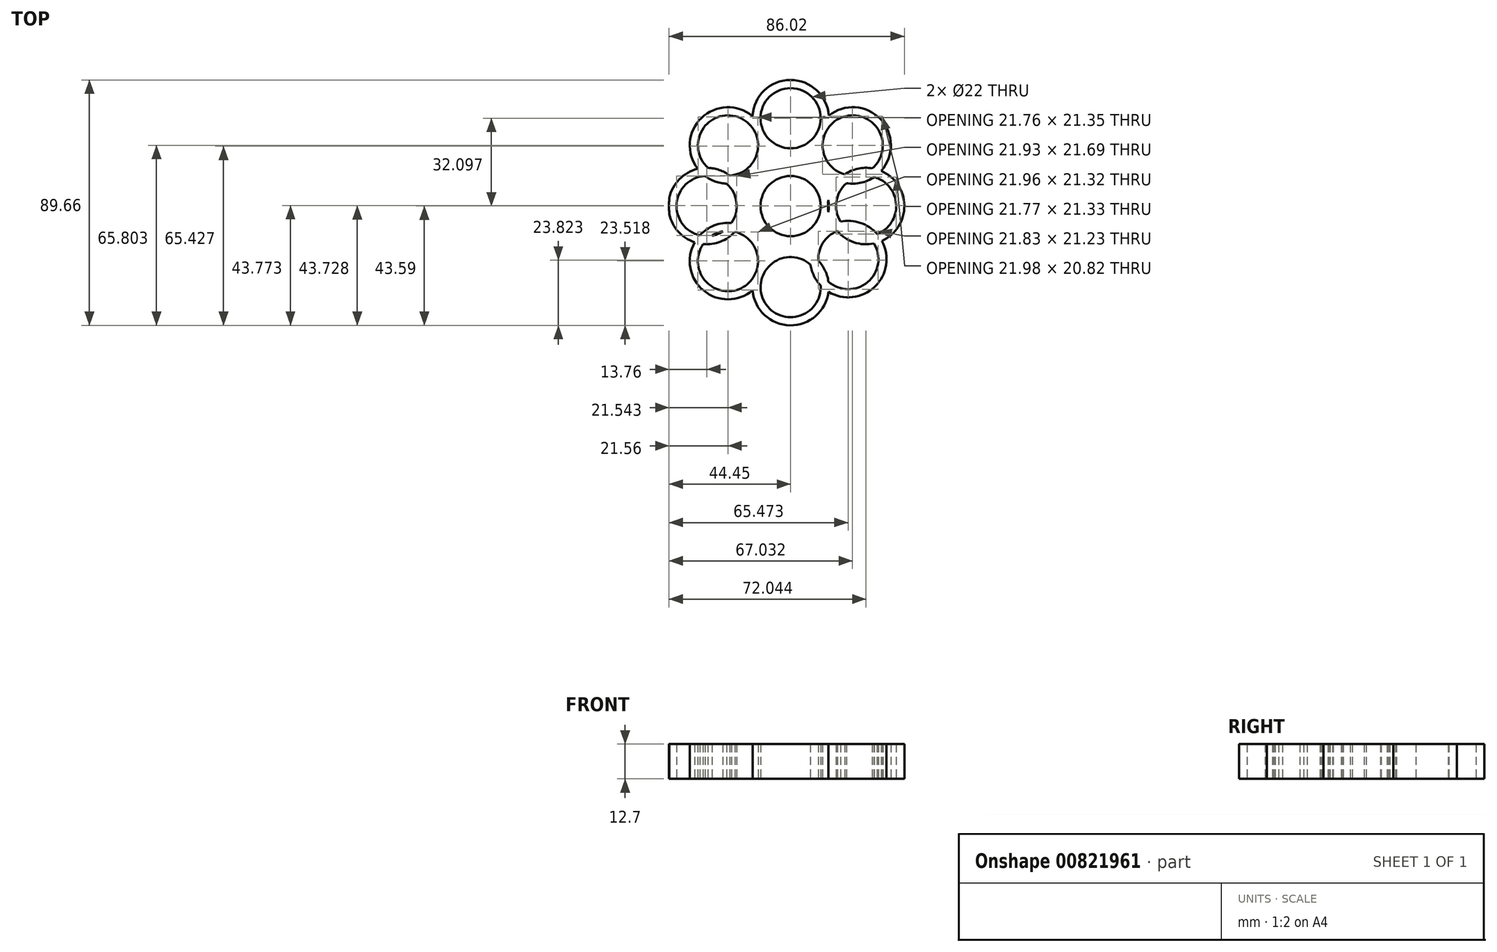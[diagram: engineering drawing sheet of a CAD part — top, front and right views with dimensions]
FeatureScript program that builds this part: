
annotation { "Feature Type Name" : "Feature", "Feature Type Description" : "" }
export const myFeature = defineFeature(function(context is Context, id is Id, definition is map)
    precondition{}
    {
        {
            var Q0;
            Q0=qCreatedBy(makeId("Top.planeOp"),FACE);
            var sketch = newSketch(context, id + "F0", { "sketchPlane" : qUnion([Q0])});
            skCircle(sketch, "E0", {"center": v(0, 0) * mm, "radius": 44.45 * mm});
            skCircle(sketch, "E1", {"center": v(0, 0) * mm, "radius": 11 * mm});
            skCircle(sketch, "E2", {"center": v(0, 32.1) * mm, "radius": 11 * mm});
            skCircle(sketch, "E3", {"center": v(-30.7, 0) * mm, "radius": 11 * mm});
            skCircle(sketch, "E4", {"center": v(27.6, 0) * mm, "radius": 11 * mm});
            skCircle(sketch, "E5", {"center": v(0, -29.62) * mm, "radius": 11 * mm});
            skCircle(sketch, "E6", {"center": v(-22.9, 22.14) * mm, "radius": 11 * mm});
            skCircle(sketch, "E7", {"center": v(22.69, 22.14) * mm, "radius": 11 * mm});
            skCircle(sketch, "E8", {"center": v(-22.9, -20.12) * mm, "radius": 11 * mm});
            skCircle(sketch, "E9", {"center": v(21.09, -19.38) * mm, "radius": 11 * mm});
            skCircle(sketch, "E10", {"center": v(0, 32.1) * mm, "radius": 13.97 * mm});
            skCircle(sketch, "E11", {"center": v(-22.9, 22.14) * mm, "radius": 13.97 * mm});
            skCircle(sketch, "E12", {"center": v(-30.7, 0) * mm, "radius": 13.97 * mm});
            skCircle(sketch, "E13", {"center": v(-22.9, -20.12) * mm, "radius": 13.97 * mm});
            skCircle(sketch, "E14", {"center": v(0, -29.62) * mm, "radius": 13.97 * mm});
            skCircle(sketch, "E15", {"center": v(21.09, -19.38) * mm, "radius": 13.97 * mm});
            skCircle(sketch, "E16", {"center": v(27.6, 0) * mm, "radius": 13.97 * mm});
            skCircle(sketch, "E17", {"center": v(22.69, 22.14) * mm, "radius": 13.97 * mm});
            skCircle(sketch, "E18", {"center": v(0, 0) * mm, "radius": 13.97 * mm});
            skArc(sketch, "E19", {"start": v(0, 13.97) * mm, "mid": v(-1.87, 16.44) * mm, "end": v(-3.99, 18.7) * mm});
            skSolve(sketch);
        }
        {
            var Q0;
            {var subQ0=sQuery(id+"F0.wireOp",EDGE,"E10");var subQ1=sQuery(id+"F0.wireOp",EDGE,"E6");var subQ2=makeQuery(id+"F0.imprint","INTERSECT",VERTEX,{"derivedFrom":[subQ1,subQ0]});Q0=makeQuery(id+"F0.imprint","IMPRINT",FACE,{"disambiguationData":[TD([[makeQuery(id+"F0.imprint","IMPRINT",EDGE,{"disambiguationData":[TD([[subQ2,1.0]])],"derivedFrom":subQ1}),-1.0]])]});}
            var Q1;
            {var subQ0=sQuery(id+"F0.wireOp",EDGE,"E12");var subQ1=sQuery(id+"F0.wireOp",EDGE,"E0");var subQ2=makeQuery(id+"F0.imprint","INTERSECT",VERTEX,{"disambiguationData":[OD(0.0)],"derivedFrom":[subQ1,subQ0]});Q1=makeQuery(id+"F0.imprint","IMPRINT",FACE,{"disambiguationData":[TD([[makeQuery(id+"F0.imprint","IMPRINT",EDGE,{"disambiguationData":[TD([[subQ2,-1.0]])],"derivedFrom":subQ1}),1.0]])]});}
            var Q2;
            {var subQ0=sQuery(id+"F0.wireOp",EDGE,"E11");var subQ1=sQuery(id+"F0.wireOp",EDGE,"E0");var subQ2=makeQuery(id+"F0.imprint","INTERSECT",VERTEX,{"disambiguationData":[OD(0.0)],"derivedFrom":[subQ1,subQ0]});Q2=makeQuery(id+"F0.imprint","IMPRINT",FACE,{"disambiguationData":[TD([[makeQuery(id+"F0.imprint","IMPRINT",EDGE,{"disambiguationData":[TD([[subQ2,-1.0]])],"derivedFrom":subQ1}),-1.0]])]});}
            var Q3;
            {var subQ3=sQuery(id+"F0.wireOp",EDGE,"E11");var subQ7=sQuery(id+"F0.wireOp",EDGE,"E0");var subQ8=makeQuery(id+"F0.imprint","INTERSECT",VERTEX,{"disambiguationData":[OD(0.0)],"derivedFrom":[subQ7,subQ3]});Q3=makeQuery(id+"F0.imprint","IMPRINT",FACE,{"disambiguationData":[TD([[makeQuery(id+"F0.imprint","IMPRINT",EDGE,{"disambiguationData":[TD([[subQ8,-1.0]])],"derivedFrom":subQ7}),1.0]])]});}
            var Q4;
            {var subQ0=sQuery(id+"F0.wireOp",EDGE,"E11");var subQ1=sQuery(id+"F0.wireOp",EDGE,"E3");var subQ5=makeQuery(id+"F0.imprint","INTERSECT",VERTEX,{"disambiguationData":[OD(0.0)],"derivedFrom":[subQ1,subQ0]});Q4=makeQuery(id+"F0.imprint","IMPRINT",FACE,{"disambiguationData":[TD([[makeQuery(id+"F0.imprint","IMPRINT",EDGE,{"disambiguationData":[TD([[subQ5,1.0]])],"derivedFrom":subQ1}),-1.0]])]});}
            var Q5;
            {var subQ0=sQuery(id+"F0.wireOp",EDGE,"E11");var subQ1=sQuery(id+"F0.wireOp",EDGE,"E3");var subQ2=makeQuery(id+"F0.imprint","INTERSECT",VERTEX,{"disambiguationData":[OD(1.0)],"derivedFrom":[subQ1,subQ0]});Q5=makeQuery(id+"F0.imprint","IMPRINT",FACE,{"disambiguationData":[TD([[makeQuery(id+"F0.imprint","IMPRINT",EDGE,{"disambiguationData":[TD([[subQ2,1.0]])],"derivedFrom":subQ1}),-1.0]])]});}
            var Q6;
            {var subQ0=sQuery(id+"F0.wireOp",EDGE,"E12");var subQ1=sQuery(id+"F0.wireOp",EDGE,"E8");var subQ2=makeQuery(id+"F0.imprint","INTERSECT",VERTEX,{"disambiguationData":[OD(0.0)],"derivedFrom":[subQ1,subQ0]});Q6=makeQuery(id+"F0.imprint","IMPRINT",FACE,{"disambiguationData":[TD([[makeQuery(id+"F0.imprint","IMPRINT",EDGE,{"disambiguationData":[TD([[subQ2,1.0]])],"derivedFrom":subQ1}),-1.0]])]});}
            var Q7;
            {var subQ0=sQuery(id+"F0.wireOp",EDGE,"E8");var subQ1=sQuery(id+"F0.wireOp",EDGE,"E3");var subQ2=makeQuery(id+"F0.imprint","INTERSECT",VERTEX,{"disambiguationData":[OD(1.0)],"derivedFrom":[subQ1,subQ0]});Q7=makeQuery(id+"F0.imprint","IMPRINT",FACE,{"disambiguationData":[TD([[makeQuery(id+"F0.imprint","IMPRINT",EDGE,{"disambiguationData":[TD([[subQ2,-1.0]])],"derivedFrom":subQ1}),-1.0]])]});}
            var Q8;
            {var subQ0=sQuery(id+"F0.wireOp",EDGE,"E13");var subQ1=sQuery(id+"F0.wireOp",EDGE,"E3");var subQ2=makeQuery(id+"F0.imprint","INTERSECT",VERTEX,{"disambiguationData":[OD(0.0)],"derivedFrom":[subQ1,subQ0]});Q8=makeQuery(id+"F0.imprint","IMPRINT",FACE,{"disambiguationData":[TD([[makeQuery(id+"F0.imprint","IMPRINT",EDGE,{"disambiguationData":[TD([[subQ2,-1.0]])],"derivedFrom":subQ1}),-1.0]])]});}
            var Q9;
            {var subQ0=sQuery(id+"F0.wireOp",EDGE,"E11");var subQ1=sQuery(id+"F0.wireOp",EDGE,"E3");var subQ2=makeQuery(id+"F0.imprint","INTERSECT",VERTEX,{"disambiguationData":[OD(0.0)],"derivedFrom":[subQ1,subQ0]});Q9=makeQuery(id+"F0.imprint","IMPRINT",FACE,{"disambiguationData":[TD([[makeQuery(id+"F0.imprint","IMPRINT",EDGE,{"disambiguationData":[TD([[subQ2,1.0]])],"derivedFrom":subQ1}),1.0]])]});}
            var Q10;
            {var subQ0=sQuery(id+"F0.wireOp",EDGE,"E12");var subQ1=sQuery(id+"F0.wireOp",EDGE,"E6");var subQ2=makeQuery(id+"F0.imprint","INTERSECT",VERTEX,{"disambiguationData":[OD(0.0)],"derivedFrom":[subQ1,subQ0]});Q10=makeQuery(id+"F0.imprint","IMPRINT",FACE,{"disambiguationData":[TD([[makeQuery(id+"F0.imprint","IMPRINT",EDGE,{"disambiguationData":[TD([[subQ2,-1.0]])],"derivedFrom":subQ1}),1.0]])]});}
            var Q11;
            {var subQ0=sQuery(id+"F0.wireOp",EDGE,"E10");var subQ1=makeQuery(id+"F0.imprint","INTERSECT",VERTEX,{"derivedFrom":[sQuery(id+"F0.wireOp",EDGE,"E6"),subQ0]});Q11=makeQuery(id+"F0.imprint","IMPRINT",FACE,{"disambiguationData":[TD([[makeQuery(id+"F0.imprint","IMPRINT",EDGE,{"disambiguationData":[TD([[subQ1,1.0]])],"derivedFrom":subQ0}),1.0]])]});}
            var Q12;
            {var subQ1=sQuery(id+"F0.wireOp",EDGE,"E2");var subQ6=sQuery(id+"F0.wireOp",EDGE,"E17");var subQ8=makeQuery(id+"F0.imprint","INTERSECT",VERTEX,{"disambiguationData":[OD(0.0)],"derivedFrom":[subQ1,subQ6]});Q12=makeQuery(id+"F0.imprint","IMPRINT",FACE,{"disambiguationData":[TD([[makeQuery(id+"F0.imprint","IMPRINT",EDGE,{"disambiguationData":[TD([[subQ8,1.0]])],"derivedFrom":subQ1}),-1.0]])]});}
            var Q13;
            {var subQ0=sQuery(id+"F0.wireOp",EDGE,"E10");var subQ1=sQuery(id+"F0.wireOp",EDGE,"E0");var subQ5=makeQuery(id+"F0.imprint","INTERSECT",VERTEX,{"disambiguationData":[OD(0.0)],"derivedFrom":[subQ1,subQ0]});Q13=makeQuery(id+"F0.imprint","IMPRINT",FACE,{"disambiguationData":[TD([[makeQuery(id+"F0.imprint","IMPRINT",EDGE,{"disambiguationData":[TD([[subQ5,-1.0]])],"derivedFrom":subQ1}),1.0]])]});}
            var Q14;
            {var subQ3=sQuery(id+"F0.wireOp",EDGE,"E17");var subQ5=sQuery(id+"F0.wireOp",EDGE,"E2");var subQ6=makeQuery(id+"F0.imprint","INTERSECT",VERTEX,{"disambiguationData":[OD(0.0)],"derivedFrom":[subQ5,subQ3]});Q14=makeQuery(id+"F0.imprint","IMPRINT",FACE,{"disambiguationData":[TD([[makeQuery(id+"F0.imprint","IMPRINT",EDGE,{"disambiguationData":[TD([[subQ6,-1.0]])],"derivedFrom":subQ5}),-1.0]])]});}
            var Q15;
            {var subQ0=sQuery(id+"F0.wireOp",EDGE,"E10");var subQ1=sQuery(id+"F0.wireOp",EDGE,"E0");var subQ2=makeQuery(id+"F0.imprint","INTERSECT",VERTEX,{"disambiguationData":[OD(0.0)],"derivedFrom":[subQ1,subQ0]});Q15=makeQuery(id+"F0.imprint","IMPRINT",FACE,{"disambiguationData":[TD([[makeQuery(id+"F0.imprint","IMPRINT",EDGE,{"disambiguationData":[TD([[subQ2,-1.0]])],"derivedFrom":subQ1}),-1.0]])]});}
            var Q16;
            {var subQ0=sQuery(id+"F0.wireOp",EDGE,"E13");var subQ1=sQuery(id+"F0.wireOp",EDGE,"E3");var subQ2=makeQuery(id+"F0.imprint","INTERSECT",VERTEX,{"disambiguationData":[OD(0.0)],"derivedFrom":[subQ1,subQ0]});Q16=makeQuery(id+"F0.imprint","IMPRINT",FACE,{"disambiguationData":[TD([[makeQuery(id+"F0.imprint","IMPRINT",EDGE,{"disambiguationData":[TD([[subQ2,-1.0]])],"derivedFrom":subQ1}),1.0]])]});}
            var Q17;
            {var subQ4=sQuery(id+"F0.wireOp",EDGE,"E12");var subQ6=sQuery(id+"F0.wireOp",EDGE,"E8");var subQ7=makeQuery(id+"F0.imprint","INTERSECT",VERTEX,{"disambiguationData":[OD(1.0)],"derivedFrom":[subQ6,subQ4]});Q17=makeQuery(id+"F0.imprint","IMPRINT",FACE,{"disambiguationData":[TD([[makeQuery(id+"F0.imprint","IMPRINT",EDGE,{"disambiguationData":[TD([[subQ7,-1.0]])],"derivedFrom":subQ6}),-1.0]])]});}
            var Q18;
            {var subQ0=sQuery(id+"F0.wireOp",EDGE,"E13");var subQ1=sQuery(id+"F0.wireOp",EDGE,"E5");var subQ5=makeQuery(id+"F0.imprint","INTERSECT",VERTEX,{"disambiguationData":[OD(0.0)],"derivedFrom":[subQ1,subQ0]});Q18=makeQuery(id+"F0.imprint","IMPRINT",FACE,{"disambiguationData":[TD([[makeQuery(id+"F0.imprint","IMPRINT",EDGE,{"disambiguationData":[TD([[subQ5,-1.0]])],"derivedFrom":subQ1}),-1.0]])]});}
            var Q19;
            {var subQ0=sQuery(id+"F0.wireOp",EDGE,"E15");var subQ1=sQuery(id+"F0.wireOp",EDGE,"E5");var subQ2=makeQuery(id+"F0.imprint","INTERSECT",VERTEX,{"disambiguationData":[OD(1.0)],"derivedFrom":[subQ1,subQ0]});Q19=makeQuery(id+"F0.imprint","IMPRINT",FACE,{"disambiguationData":[TD([[makeQuery(id+"F0.imprint","IMPRINT",EDGE,{"disambiguationData":[TD([[subQ2,1.0]])],"derivedFrom":subQ1}),-1.0]])]});}
            var Q20;
            {var subQ0=sQuery(id+"F0.wireOp",EDGE,"E14");var subQ1=sQuery(id+"F0.wireOp",EDGE,"E9");var subQ2=makeQuery(id+"F0.imprint","INTERSECT",VERTEX,{"disambiguationData":[OD(0.0)],"derivedFrom":[subQ1,subQ0]});Q20=makeQuery(id+"F0.imprint","IMPRINT",FACE,{"disambiguationData":[TD([[makeQuery(id+"F0.imprint","IMPRINT",EDGE,{"disambiguationData":[TD([[subQ2,-1.0]])],"derivedFrom":subQ1}),1.0]])]});}
            var Q21;
            {var subQ0=sQuery(id+"F0.wireOp",EDGE,"E15");var subQ1=sQuery(id+"F0.wireOp",EDGE,"E5");var subQ2=makeQuery(id+"F0.imprint","INTERSECT",VERTEX,{"disambiguationData":[OD(0.0)],"derivedFrom":[subQ1,subQ0]});Q21=makeQuery(id+"F0.imprint","IMPRINT",FACE,{"disambiguationData":[TD([[makeQuery(id+"F0.imprint","IMPRINT",EDGE,{"disambiguationData":[TD([[subQ2,-1.0]])],"derivedFrom":subQ1}),-1.0]])]});}
            var Q22;
            {var subQ3=sQuery(id+"F0.wireOp",EDGE,"E15");var subQ7=sQuery(id+"F0.wireOp",EDGE,"E5");var subQ8=makeQuery(id+"F0.imprint","INTERSECT",VERTEX,{"disambiguationData":[OD(0.0)],"derivedFrom":[subQ7,subQ3]});Q22=makeQuery(id+"F0.imprint","IMPRINT",FACE,{"disambiguationData":[TD([[makeQuery(id+"F0.imprint","IMPRINT",EDGE,{"disambiguationData":[TD([[subQ8,1.0]])],"derivedFrom":subQ7}),-1.0]])]});}
            var Q23;
            {var subQ0=sQuery(id+"F0.wireOp",EDGE,"E16");var subQ1=sQuery(id+"F0.wireOp",EDGE,"E9");var subQ2=makeQuery(id+"F0.imprint","INTERSECT",VERTEX,{"disambiguationData":[OD(0.0)],"derivedFrom":[subQ1,subQ0]});Q23=makeQuery(id+"F0.imprint","IMPRINT",FACE,{"disambiguationData":[TD([[makeQuery(id+"F0.imprint","IMPRINT",EDGE,{"disambiguationData":[TD([[subQ2,1.0]])],"derivedFrom":subQ1}),-1.0]])]});}
            var Q24;
            {var subQ0=sQuery(id+"F0.wireOp",EDGE,"E15");var subQ1=sQuery(id+"F0.wireOp",EDGE,"E5");var subQ2=makeQuery(id+"F0.imprint","INTERSECT",VERTEX,{"disambiguationData":[OD(0.0)],"derivedFrom":[subQ1,subQ0]});Q24=makeQuery(id+"F0.imprint","IMPRINT",FACE,{"disambiguationData":[TD([[makeQuery(id+"F0.imprint","IMPRINT",EDGE,{"disambiguationData":[TD([[subQ2,1.0]])],"derivedFrom":subQ1}),1.0]])]});}
            var Q25;
            {var subQ0=sQuery(id+"F0.wireOp",EDGE,"E16");var subQ1=sQuery(id+"F0.wireOp",EDGE,"E9");var subQ2=makeQuery(id+"F0.imprint","INTERSECT",VERTEX,{"disambiguationData":[OD(1.0)],"derivedFrom":[subQ1,subQ0]});Q25=makeQuery(id+"F0.imprint","IMPRINT",FACE,{"disambiguationData":[TD([[makeQuery(id+"F0.imprint","IMPRINT",EDGE,{"disambiguationData":[TD([[subQ2,-1.0]])],"derivedFrom":subQ1}),-1.0]])]});}
            var Q26;
            {var subQ0=sQuery(id+"F0.wireOp",EDGE,"E15");var subQ1=sQuery(id+"F0.wireOp",EDGE,"E4");var subQ2=makeQuery(id+"F0.imprint","INTERSECT",VERTEX,{"disambiguationData":[OD(0.0)],"derivedFrom":[subQ1,subQ0]});Q26=makeQuery(id+"F0.imprint","IMPRINT",FACE,{"disambiguationData":[TD([[makeQuery(id+"F0.imprint","IMPRINT",EDGE,{"disambiguationData":[TD([[subQ2,-1.0]])],"derivedFrom":subQ1}),1.0]])]});}
            var Q27;
            {var subQ0=sQuery(id+"F0.wireOp",EDGE,"E9");var subQ1=sQuery(id+"F0.wireOp",EDGE,"E4");var subQ2=makeQuery(id+"F0.imprint","INTERSECT",VERTEX,{"disambiguationData":[OD(0.0)],"derivedFrom":[subQ1,subQ0]});Q27=makeQuery(id+"F0.imprint","IMPRINT",FACE,{"disambiguationData":[TD([[makeQuery(id+"F0.imprint","IMPRINT",EDGE,{"disambiguationData":[TD([[subQ2,-1.0]])],"derivedFrom":subQ1}),-1.0]])]});}
            var Q28;
            {var subQ0=sQuery(id+"F0.wireOp",EDGE,"E15");var subQ1=sQuery(id+"F0.wireOp",EDGE,"E4");var subQ2=makeQuery(id+"F0.imprint","INTERSECT",VERTEX,{"disambiguationData":[OD(0.0)],"derivedFrom":[subQ1,subQ0]});Q28=makeQuery(id+"F0.imprint","IMPRINT",FACE,{"disambiguationData":[TD([[makeQuery(id+"F0.imprint","IMPRINT",EDGE,{"disambiguationData":[TD([[subQ2,-1.0]])],"derivedFrom":subQ1}),-1.0]])]});}
            var Q29;
            {var subQ0=sQuery(id+"F0.wireOp",EDGE,"E17");var subQ1=sQuery(id+"F0.wireOp",EDGE,"E4");var subQ2=makeQuery(id+"F0.imprint","INTERSECT",VERTEX,{"disambiguationData":[OD(1.0)],"derivedFrom":[subQ1,subQ0]});Q29=makeQuery(id+"F0.imprint","IMPRINT",FACE,{"disambiguationData":[TD([[makeQuery(id+"F0.imprint","IMPRINT",EDGE,{"disambiguationData":[TD([[subQ2,1.0]])],"derivedFrom":subQ1}),-1.0]])]});}
            var Q30;
            {var subQ0=sQuery(id+"F0.wireOp",EDGE,"E16");var subQ1=sQuery(id+"F0.wireOp",EDGE,"E7");var subQ2=makeQuery(id+"F0.imprint","INTERSECT",VERTEX,{"disambiguationData":[OD(0.0)],"derivedFrom":[subQ1,subQ0]});Q30=makeQuery(id+"F0.imprint","IMPRINT",FACE,{"disambiguationData":[TD([[makeQuery(id+"F0.imprint","IMPRINT",EDGE,{"disambiguationData":[TD([[subQ2,-1.0]])],"derivedFrom":subQ1}),1.0]])]});}
            var Q31;
            {var subQ5=sQuery(id+"F0.wireOp",EDGE,"E4");var subQ7=sQuery(id+"F0.wireOp",EDGE,"E17");var subQ8=makeQuery(id+"F0.imprint","INTERSECT",VERTEX,{"disambiguationData":[OD(0.0)],"derivedFrom":[subQ5,subQ7]});Q31=makeQuery(id+"F0.imprint","IMPRINT",FACE,{"disambiguationData":[TD([[makeQuery(id+"F0.imprint","IMPRINT",EDGE,{"disambiguationData":[TD([[subQ8,-1.0]])],"derivedFrom":subQ5}),-1.0]])]});}
            var Q32;
            {var subQ3=sQuery(id+"F0.wireOp",EDGE,"E17");var subQ7=sQuery(id+"F0.wireOp",EDGE,"E4");var subQ8=makeQuery(id+"F0.imprint","INTERSECT",VERTEX,{"disambiguationData":[OD(0.0)],"derivedFrom":[subQ7,subQ3]});Q32=makeQuery(id+"F0.imprint","IMPRINT",FACE,{"disambiguationData":[TD([[makeQuery(id+"F0.imprint","IMPRINT",EDGE,{"disambiguationData":[TD([[subQ8,1.0]])],"derivedFrom":subQ7}),-1.0]])]});}
            var Q33;
            {var subQ3=sQuery(id+"F0.wireOp",EDGE,"E17");var subQ5=sQuery(id+"F0.wireOp",EDGE,"E0");var subQ6=makeQuery(id+"F0.imprint","INTERSECT",VERTEX,{"disambiguationData":[OD(0.0)],"derivedFrom":[subQ5,subQ3]});Q33=makeQuery(id+"F0.imprint","IMPRINT",FACE,{"disambiguationData":[TD([[makeQuery(id+"F0.imprint","IMPRINT",EDGE,{"disambiguationData":[TD([[subQ6,1.0]])],"derivedFrom":subQ5}),1.0]])]});}
            var Q34;
            {var subQ0=sQuery(id+"F0.wireOp",EDGE,"E10");var subQ1=sQuery(id+"F0.wireOp",EDGE,"E7");var subQ2=makeQuery(id+"F0.imprint","INTERSECT",VERTEX,{"disambiguationData":[OD(0.0)],"derivedFrom":[subQ1,subQ0]});Q34=makeQuery(id+"F0.imprint","IMPRINT",FACE,{"disambiguationData":[TD([[makeQuery(id+"F0.imprint","IMPRINT",EDGE,{"disambiguationData":[TD([[subQ2,-1.0]])],"derivedFrom":subQ1}),-1.0]])]});}
            var Q35;
            {var subQ0=sQuery(id+"F0.wireOp",EDGE,"E17");var subQ1=sQuery(id+"F0.wireOp",EDGE,"E0");var subQ2=makeQuery(id+"F0.imprint","INTERSECT",VERTEX,{"disambiguationData":[OD(0.0)],"derivedFrom":[subQ1,subQ0]});Q35=makeQuery(id+"F0.imprint","IMPRINT",FACE,{"disambiguationData":[TD([[makeQuery(id+"F0.imprint","IMPRINT",EDGE,{"disambiguationData":[TD([[subQ2,1.0]])],"derivedFrom":subQ1}),-1.0]])]});}
            var Q36;
            Q36=makeQuery(id+"F0.imprint","IMPRINT",FACE,{"disambiguationData":[TD([[makeQuery(id+"F0.imprint","IMPRINT",EDGE,{"derivedFrom":sQuery(id+"F0.wireOp",EDGE,"E1")}),-1.0]])]});
            var Q37;
            {var subQ0=sQuery(id+"F0.wireOp",EDGE,"E9");var subQ1=sQuery(id+"F0.wireOp",EDGE,"E4");var subQ2=makeQuery(id+"F0.imprint","INTERSECT",VERTEX,{"disambiguationData":[OD(1.0)],"derivedFrom":[subQ1,subQ0]});Q37=makeQuery(id+"F0.imprint","IMPRINT",FACE,{"disambiguationData":[TD([[makeQuery(id+"F0.imprint","IMPRINT",EDGE,{"disambiguationData":[TD([[subQ2,-1.0]])],"derivedFrom":subQ1}),-1.0]])]});}
            var Q38;
            {var subQ0=sQuery(id+"F0.wireOp",EDGE,"E17");var subQ1=sQuery(id+"F0.wireOp",EDGE,"E4");var subQ2=makeQuery(id+"F0.imprint","INTERSECT",VERTEX,{"disambiguationData":[OD(0.0)],"derivedFrom":[subQ1,subQ0]});Q38=makeQuery(id+"F0.imprint","IMPRINT",FACE,{"disambiguationData":[TD([[makeQuery(id+"F0.imprint","IMPRINT",EDGE,{"disambiguationData":[TD([[subQ2,1.0]])],"derivedFrom":subQ1}),1.0]])]});}
            var Q39;
            {var subQ0=sQuery(id+"F0.wireOp",EDGE,"E9");var subQ1=sQuery(id+"F0.wireOp",EDGE,"E4");var subQ2=makeQuery(id+"F0.imprint","INTERSECT",VERTEX,{"disambiguationData":[OD(0.0)],"derivedFrom":[subQ1,subQ0]});Q39=makeQuery(id+"F0.imprint","IMPRINT",FACE,{"disambiguationData":[TD([[makeQuery(id+"F0.imprint","IMPRINT",EDGE,{"disambiguationData":[TD([[subQ2,-1.0]])],"derivedFrom":subQ1}),1.0]])]});}
            var Q40;
            {var subQ0=sQuery(id+"F0.wireOp",EDGE,"E8");var subQ1=sQuery(id+"F0.wireOp",EDGE,"E3");var subQ2=makeQuery(id+"F0.imprint","INTERSECT",VERTEX,{"disambiguationData":[OD(0.0)],"derivedFrom":[subQ1,subQ0]});Q40=makeQuery(id+"F0.imprint","IMPRINT",FACE,{"disambiguationData":[TD([[makeQuery(id+"F0.imprint","IMPRINT",EDGE,{"disambiguationData":[TD([[subQ2,-1.0]])],"derivedFrom":subQ1}),-1.0]])]});}
            var Q41;
            {var subQ0=sQuery(id+"F0.wireOp",EDGE,"E19");Q41=makeQuery(id+"F0.imprint","IMPRINT",FACE,{"disambiguationData":[TD([[makeQuery(id+"F0.imprint","IMPRINT",EDGE,{"derivedFrom":subQ0}),-1.0]])]});}
            var Q42;
            {var subQ11=sQuery(id+"F0.wireOp",EDGE,"E19");Q42=makeQuery(id+"F0.imprint","IMPRINT",FACE,{"disambiguationData":[TD([[makeQuery(id+"F0.imprint","IMPRINT",EDGE,{"derivedFrom":subQ11}),1.0]])]});}
            extrude(context, id + "F1", {"entities" : qUnion([Q0, Q1, Q2, Q3, Q4, Q5, Q6, Q7, Q8, Q9, Q10, Q11, Q12, Q13, Q14, Q15, Q16, Q17, Q18, Q19, Q20, Q21, Q22, Q23, Q24, Q25, Q26, Q27, Q28, Q29, Q30, Q31, Q32, Q33, Q34, Q35, Q36, Q37, Q38, Q39, Q40, Q41, Q42]), "depth" : 12.7 * mm, "offsetDistance" : 25.4 * mm});
        }
    });
